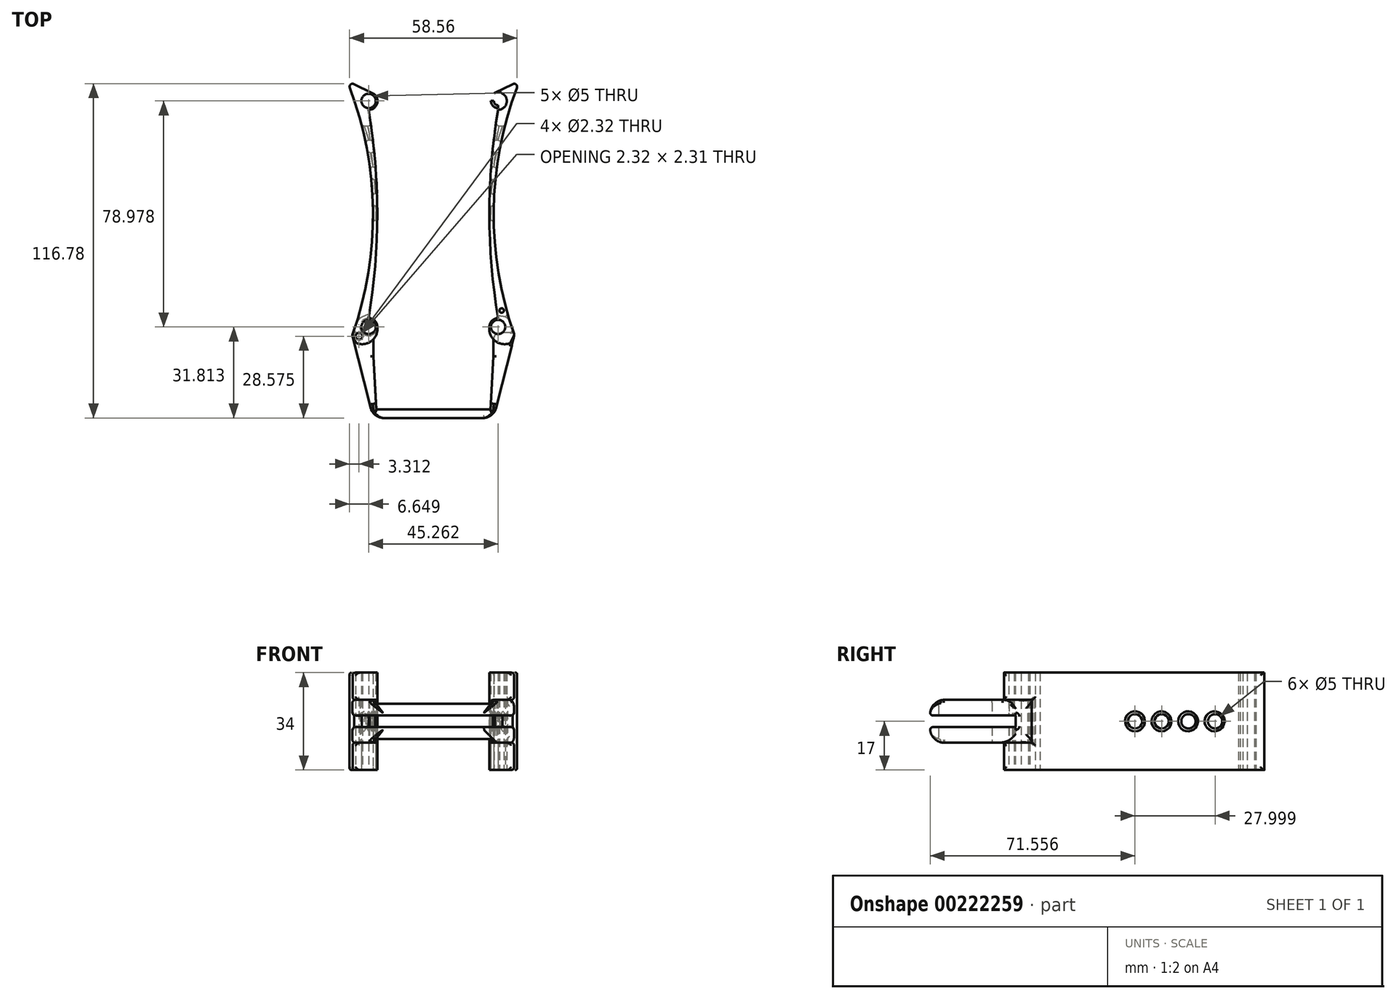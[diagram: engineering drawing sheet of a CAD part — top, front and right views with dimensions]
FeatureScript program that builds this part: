
annotation { "Feature Type Name" : "Feature", "Feature Type Description" : "" }
export const myFeature = defineFeature(function(context is Context, id is Id, definition is map)
    precondition{}
    {
        {
            var Q0;
            Q0=qCreatedBy(makeId("Top.planeOp"),FACE);
            var sketch = newSketch(context, id + "F0", { "sketchPlane" : qUnion([Q0])});
            skPoint(sketch, "E0.middle", {"position": v(-0.14, 7.73) * mm});
            skCircle(sketch, "E1", {"center": v(-22.63, 47.23) * mm, "radius": 1.5 * mm});
            skCircle(sketch, "E2", {"center": v(-22.63, -31.75) * mm, "radius": 1.5 * mm});
            skLineSegment(sketch, "E3.MirrorCS", {"start": v(-28.32, -34.53) * mm, "end": v(-26.94, -37.37) * mm});
            skPoint(sketch, "E4.orphan", {"position": v(-30.14, -38.77) * mm});
            skCircle(sketch, "E5", {"center": v(-22.63, 47.23) * mm, "radius": 2.5 * mm});
            skCircle(sketch, "E6", {"center": v(-22.63, -31.75) * mm, "radius": 2.5 * mm});
            skLineSegment(sketch, "E7.bottom", {"start": v(-22.63, 47.23) * mm, "end": v(-20.13, 47.23) * mm});
            skLineSegment(sketch, "E7.top", {"start": v(-22.63, -31.77) * mm, "end": v(-20.13, -31.77) * mm});
            skLineSegment(sketch, "E7.left", {"start": v(-22.63, 47.23) * mm, "end": v(-22.63, 44.73) * mm});
            skLineSegment(sketch, "E8.trimOffspring", {"start": v(-22.63, -29.25) * mm, "end": v(-22.63, -31.77) * mm});
            skCircle(sketch, "E9", {"center": v(-17.26, 14.85) * mm, "radius": 1.49 * mm});
            skPoint(sketch, "E10.visualSharp", {"position": v(-16.9, 52.24) * mm});
            skPoint(sketch, "E11.visualSharp", {"position": v(-16.9, -36.79) * mm});
            skPoint(sketch, "E12.orphan", {"position": v(-25.56, -40.21) * mm});
            skLineSegment(sketch, "E13", {"start": v(0, 54.23) * mm, "end": v(0, -41.79) * mm});
            skCircle(sketch, "E14", {"center": v(-22.63, -31.75) * mm, "radius": 3.07 * mm});
            skCircle(sketch, "E15", {"center": v(-22.6, 47.19) * mm, "radius": 3.07 * mm});
            skLineSegment(sketch, "E16", {"start": v(-30.13, 54.23) * mm, "end": v(-21.26, 49.95) * mm});
            skArc(sketch, "E17", {"start": v(-22.63, -28.68) * mm, "mid": v(-19.57, 7.72) * mm, "end": v(-22.63, 44.12) * mm});
            skArc(sketch, "E18", {"start": v(-28.32, -34.53) * mm, "mid": v(-21.12, 10.01) * mm, "end": v(-30.13, 54.23) * mm});
            skArc(sketch, "E19", {"start": v(-26.94, -37.37) * mm, "mid": v(-21.67, -36.68) * mm, "end": v(-19.57, -31.79) * mm});
            skCircle(sketch, "E20", {"center": v(-25.97, -34.98) * mm, "radius": 1.16 * mm});
            skLineSegment(sketch, "E21", {"start": v(-20.93, -41.99) * mm, "end": v(-21.06, -41.99) * mm});
            skLineSegment(sketch, "E22", {"start": v(-0.03, 54.43) * mm, "end": v(-0.03, -55.57) * mm});
            skLineSegment(sketch, "E23.bottom", {"start": v(17.94, -58.7) * mm, "end": v(-18, -58.7) * mm});
            skLineSegment(sketch, "E23.top", {"start": v(17.94, -25.28) * mm, "end": v(-18, -25.28) * mm});
            skLineSegment(sketch, "E23.left", {"start": v(17.94, -58.7) * mm, "end": v(17.94, -25.28) * mm});
            skLineSegment(sketch, "E23.right", {"start": v(-18, -58.7) * mm, "end": v(-18, -25.28) * mm});
            skPoint(sketch, "E23.middle", {"position": v(-0.03, -41.99) * mm});
            skLineSegment(sketch, "E24", {"start": v(-21.06, -63.6) * mm, "end": v(1.55, -63.6) * mm});
            skLineSegment(sketch, "E25", {"start": v(-19.96, -60.6) * mm, "end": v(-20.93, -41.99) * mm});
            skLineSegment(sketch, "E26", {"start": v(-19.96, -60.6) * mm, "end": v(1.54, -60.6) * mm});
            skLineSegment(sketch, "E27.MirrorCS", {"start": v(21.06, -63.6) * mm, "end": v(-0.04, -63.6) * mm});
            skLineSegment(sketch, "E28.MirrorCS", {"start": v(19.9, -60.6) * mm, "end": v(-0.03, -60.6) * mm});
            skLineSegment(sketch, "E29.MirrorCS", {"start": v(19.9, -60.6) * mm, "end": v(20.86, -41.99) * mm});
            skLineSegment(sketch, "E30", {"start": v(-28.32, -34.53) * mm, "end": v(-21.06, -63.6) * mm});
            skLineSegment(sketch, "E31", {"start": v(-20.93, -41.99) * mm, "end": v(-20.93, -36) * mm});
            skLineSegment(sketch, "E32.MirrorCS", {"start": v(21.06, -63.6) * mm, "end": v(-1.55, -63.6) * mm});
            skLineSegment(sketch, "E33.MirrorCS", {"start": v(22.63, 47.23) * mm, "end": v(20.13, 47.23) * mm});
            skLineSegment(sketch, "E34.MirrorCS", {"start": v(22.63, -31.77) * mm, "end": v(20.13, -31.77) * mm});
            skLineSegment(sketch, "E35.MirrorCS", {"start": v(22.63, 47.23) * mm, "end": v(22.63, 44.73) * mm});
            skLineSegment(sketch, "E36.MirrorCS", {"start": v(22.63, -29.25) * mm, "end": v(22.63, -31.77) * mm});
            skCircle(sketch, "E37.MirrorC", {"center": v(22.63, 47.23) * mm, "radius": 1.5 * mm});
            skCircle(sketch, "E38.MirrorC", {"center": v(22.63, -31.75) * mm, "radius": 1.5 * mm});
            skLineSegment(sketch, "E39.MirrorCS", {"start": v(28.32, -34.53) * mm, "end": v(26.94, -37.37) * mm});
            skLineSegment(sketch, "E40.MirrorCS", {"start": v(20.93, -41.99) * mm, "end": v(21.06, -41.99) * mm});
            skCircle(sketch, "E41.MirrorC", {"center": v(22.63, 47.23) * mm, "radius": 2.5 * mm});
            skCircle(sketch, "E42.MirrorC", {"center": v(22.63, -31.75) * mm, "radius": 2.5 * mm});
            skArc(sketch, "E43.MirrorCS", {"start": v(26.94, -37.37) * mm, "mid": v(21.67, -36.68) * mm, "end": v(19.57, -31.79) * mm});
            skCircle(sketch, "E44.MirrorC", {"center": v(17.26, 14.85) * mm, "radius": 1.49 * mm});
            skPoint(sketch, "E45.MirrorP", {"position": v(30.14, -38.77) * mm});
            skCircle(sketch, "E46.MirrorC", {"center": v(22.6, 47.19) * mm, "radius": 3.07 * mm});
            skLineSegment(sketch, "E47.MirrorCS", {"start": v(20.93, -41.99) * mm, "end": v(20.93, -36) * mm});
            skCircle(sketch, "E48.MirrorC", {"center": v(22.63, -31.75) * mm, "radius": 3.07 * mm});
            skPoint(sketch, "E49.MirrorP", {"position": v(16.9, -36.79) * mm});
            skPoint(sketch, "E50.MirrorP", {"position": v(16.9, 52.24) * mm});
            skLineSegment(sketch, "E51.MirrorCS", {"start": v(30.13, 54.23) * mm, "end": v(21.26, 49.95) * mm});
            skArc(sketch, "E52.MirrorCS", {"start": v(28.32, -34.53) * mm, "mid": v(21.12, 10.01) * mm, "end": v(30.13, 54.23) * mm});
            skArc(sketch, "E53.MirrorCS", {"start": v(22.63, -28.68) * mm, "mid": v(19.57, 7.72) * mm, "end": v(22.63, 44.12) * mm});
            skLineSegment(sketch, "E54.MirrorCS", {"start": v(28.32, -34.53) * mm, "end": v(21.06, -63.6) * mm});
            skPoint(sketch, "E55.MirrorP", {"position": v(25.56, -40.21) * mm});
            skLineSegment(sketch, "E56.MirrorCS", {"start": v(19.96, -60.6) * mm, "end": v(-1.54, -60.6) * mm});
            skLineSegment(sketch, "E57.MirrorCS", {"start": v(19.96, -60.6) * mm, "end": v(20.93, -41.99) * mm});
            skLineSegment(sketch, "E58", {"start": v(-22.37, -27.13) * mm, "end": v(-25.55, -28.61) * mm});
            skLineSegment(sketch, "E59", {"start": v(-25.55, -28.61) * mm, "end": v(-26.89, -30.25) * mm});
            skLineSegment(sketch, "E60", {"start": v(20.83, -29.27) * mm, "end": v(21.44, -29.55) * mm});
            skLineSegment(sketch, "E61", {"start": v(21.5, -34.6) * mm, "end": v(22.1, -34.2) * mm});
            skLineSegment(sketch, "E62", {"start": v(20.66, -29.4) * mm, "end": v(22.63, -27.74) * mm});
            skLineSegment(sketch, "E63", {"start": v(22.63, -27.74) * mm, "end": v(26.28, -28.27) * mm});
            skLineSegment(sketch, "E64", {"start": v(21.5, -34.6) * mm, "end": v(20.93, -36) * mm});
            skCircle(sketch, "E65", {"center": v(23.85, -26) * mm, "radius": 0.78 * mm});
            skSolve(sketch);
        }
        {
            var Q0;
            Q0=makeQuery(id+"F0.imprint","IMPRINT",FACE,{"disambiguationData":[TD([[makeQuery(id+"F0.imprint","IMPRINT",EDGE,{"derivedFrom":sQuery(id+"F0.wireOp",EDGE,"E3.MirrorCS")}),1.0]])]});
            var Q1;
            {var subQ0=sQuery(id+"F0.wireOp",EDGE,"E6");var subQ1=makeQuery(id+"F0.imprint","INTERSECT",VERTEX,{"derivedFrom":[subQ0,sQuery(id+"F0.wireOp",EDGE,"E7.top")]});Q1=makeQuery(id+"F0.imprint","IMPRINT",FACE,{"disambiguationData":[TD([[makeQuery(id+"F0.imprint","IMPRINT",EDGE,{"disambiguationData":[TD([[subQ1,1.0]])],"derivedFrom":subQ0}),-1.0]])]});}
            var Q2;
            {var subQ0=sQuery(id+"F0.wireOp",EDGE,"E5");var subQ1=makeQuery(id+"F0.imprint","INTERSECT",VERTEX,{"derivedFrom":[subQ0,sQuery(id+"F0.wireOp",EDGE,"E7.bottom")]});Q2=makeQuery(id+"F0.imprint","IMPRINT",FACE,{"disambiguationData":[TD([[makeQuery(id+"F0.imprint","IMPRINT",EDGE,{"disambiguationData":[TD([[subQ1,-1.0]])],"derivedFrom":subQ0}),-1.0]])]});}
            var Q3;
            {var subQ1=sQuery(id+"F0.wireOp",EDGE,"E16");Q3=makeQuery(id+"F0.imprint","IMPRINT",FACE,{"disambiguationData":[TD([[makeQuery(id+"F0.imprint","IMPRINT",EDGE,{"derivedFrom":subQ1}),-1.0]])]});}
            var Q4;
            {var subQ6=sQuery(id+"F0.wireOp",EDGE,"E51.MirrorCS");Q4=makeQuery(id+"F0.imprint","IMPRINT",FACE,{"disambiguationData":[TD([[makeQuery(id+"F0.imprint","IMPRINT",EDGE,{"derivedFrom":subQ6}),1.0]])]});}
            var Q5;
            {var subQ0=sQuery(id+"F0.wireOp",EDGE,"E41.MirrorC");var subQ1=makeQuery(id+"F0.imprint","INTERSECT",VERTEX,{"derivedFrom":[sQuery(id+"F0.wireOp",EDGE,"E33.MirrorCS"),subQ0]});Q5=makeQuery(id+"F0.imprint","IMPRINT",FACE,{"disambiguationData":[TD([[makeQuery(id+"F0.imprint","IMPRINT",EDGE,{"disambiguationData":[TD([[subQ1,-1.0]])],"derivedFrom":subQ0}),1.0]])]});}
            var Q6;
            {var subQ1=sQuery(id+"F0.wireOp",EDGE,"E39.MirrorCS");Q6=makeQuery(id+"F0.imprint","IMPRINT",FACE,{"disambiguationData":[TD([[makeQuery(id+"F0.imprint","IMPRINT",EDGE,{"derivedFrom":subQ1}),-1.0]])]});}
            var Q7;
            {var subQ3=sQuery(id+"F0.wireOp",EDGE,"E60");Q7=makeQuery(id+"F0.imprint","IMPRINT",FACE,{"disambiguationData":[TD([[makeQuery(id+"F0.imprint","IMPRINT",EDGE,{"derivedFrom":subQ3}),1.0]])]});}
            var Q8;
            {var subQ3=sQuery(id+"F0.wireOp",EDGE,"E60");Q8=makeQuery(id+"F0.imprint","IMPRINT",FACE,{"disambiguationData":[TD([[makeQuery(id+"F0.imprint","IMPRINT",EDGE,{"derivedFrom":subQ3}),-1.0]])]});}
            var Q9;
            {var subQ0=sQuery(id+"F0.wireOp",EDGE,"E48.MirrorC");var subQ1=makeQuery(id+"F0.imprint","INTERSECT",VERTEX,{"derivedFrom":[subQ0,sQuery(id+"F0.wireOp",EDGE,"E60")]});Q9=makeQuery(id+"F0.imprint","IMPRINT",FACE,{"disambiguationData":[TD([[makeQuery(id+"F0.imprint","IMPRINT",EDGE,{"disambiguationData":[TD([[subQ1,1.0]])],"derivedFrom":subQ0}),1.0]])]});}
            var Q10;
            {var subQ3=sQuery(id+"F0.wireOp",EDGE,"E64");Q10=makeQuery(id+"F0.imprint","IMPRINT",FACE,{"disambiguationData":[TD([[makeQuery(id+"F0.imprint","IMPRINT",EDGE,{"derivedFrom":subQ3}),-1.0]])]});}
            extrude(context, id + "F1", {"entities" : qUnion([Q0, Q1, Q2, Q3, Q4, Q5, Q6, Q7, Q8, Q9, Q10]), "endBound" : BoundingType.SYMMETRIC, "depth" : 34 * mm});
        }
        {
            var Q0;
            {var subQ0=sQuery(id+"F0.wireOp",EDGE,"E6");var subQ1=makeQuery(id+"F0.imprint","INTERSECT",VERTEX,{"derivedFrom":[subQ0,sQuery(id+"F0.wireOp",EDGE,"E7.top")]});Q0=makeQuery(id+"F0.imprint","IMPRINT",FACE,{"disambiguationData":[TD([[makeQuery(id+"F0.imprint","IMPRINT",EDGE,{"disambiguationData":[TD([[subQ1,1.0]])],"derivedFrom":subQ0}),-1.0]])]});}
            var Q1;
            {var subQ1=sQuery(id+"F0.wireOp",EDGE,"E3.MirrorCS");Q1=makeQuery(id+"F0.imprint","IMPRINT",FACE,{"disambiguationData":[TD([[makeQuery(id+"F0.imprint","IMPRINT",EDGE,{"derivedFrom":subQ1}),1.0]])]});}
            var Q2;
            {var subQ0=sQuery(id+"F0.wireOp",EDGE,"E48.MirrorC");var subQ1=makeQuery(id+"F0.imprint","INTERSECT",VERTEX,{"derivedFrom":[subQ0,sQuery(id+"F0.wireOp",EDGE,"E60")]});Q2=makeQuery(id+"F0.imprint","IMPRINT",FACE,{"disambiguationData":[TD([[makeQuery(id+"F0.imprint","IMPRINT",EDGE,{"disambiguationData":[TD([[subQ1,1.0]])],"derivedFrom":subQ0}),1.0]])]});}
            var Q3;
            {var subQ1=sQuery(id+"F0.wireOp",EDGE,"E39.MirrorCS");Q3=makeQuery(id+"F0.imprint","IMPRINT",FACE,{"disambiguationData":[TD([[makeQuery(id+"F0.imprint","IMPRINT",EDGE,{"derivedFrom":subQ1}),-1.0]])]});}
            var Q4;
            {var subQ3=sQuery(id+"F0.wireOp",EDGE,"E60");Q4=makeQuery(id+"F0.imprint","IMPRINT",FACE,{"disambiguationData":[TD([[makeQuery(id+"F0.imprint","IMPRINT",EDGE,{"derivedFrom":subQ3}),1.0]])]});}
            var Q5;
            {var subQ3=sQuery(id+"F0.wireOp",EDGE,"E64");Q5=makeQuery(id+"F0.imprint","IMPRINT",FACE,{"disambiguationData":[TD([[makeQuery(id+"F0.imprint","IMPRINT",EDGE,{"derivedFrom":subQ3}),-1.0]])]});}
            var Q6;
            {var subQ3=sQuery(id+"F0.wireOp",EDGE,"E60");Q6=makeQuery(id+"F0.imprint","IMPRINT",FACE,{"disambiguationData":[TD([[makeQuery(id+"F0.imprint","IMPRINT",EDGE,{"derivedFrom":subQ3}),-1.0]])]});}
            extrude(context, id + "F2", {"entities" : qUnion([Q0, Q1, Q2, Q3, Q4, Q5, Q6]), "operationType" : NewBodyOperationType.REMOVE, "endBound" : BoundingType.SYMMETRIC, "depth" : 15 * mm});
        }
        {
            var Q0;
            {var subQ1=sQuery(id+"F0.wireOp",EDGE,"E3.MirrorCS");Q0=makeQuery(id+"F0.imprint","IMPRINT",FACE,{"disambiguationData":[TD([[makeQuery(id+"F0.imprint","IMPRINT",EDGE,{"derivedFrom":subQ1}),1.0]])]});}
            var Q1;
            {var subQ4=sQuery(id+"F0.wireOp",EDGE,"E3.MirrorCS");Q1=makeQuery(id+"F0.imprint","IMPRINT",FACE,{"disambiguationData":[TD([[makeQuery(id+"F0.imprint","IMPRINT",EDGE,{"derivedFrom":subQ4}),-1.0]])]});}
            var Q2;
            {var subQ1=sQuery(id+"F0.wireOp",EDGE,"E39.MirrorCS");Q2=makeQuery(id+"F0.imprint","IMPRINT",FACE,{"disambiguationData":[TD([[makeQuery(id+"F0.imprint","IMPRINT",EDGE,{"derivedFrom":subQ1}),-1.0]])]});}
            var Q3;
            {var subQ0=sQuery(id+"F0.wireOp",EDGE,"E48.MirrorC");var subQ1=makeQuery(id+"F0.imprint","INTERSECT",VERTEX,{"derivedFrom":[subQ0,sQuery(id+"F0.wireOp",EDGE,"E60")]});Q3=makeQuery(id+"F0.imprint","IMPRINT",FACE,{"disambiguationData":[TD([[makeQuery(id+"F0.imprint","IMPRINT",EDGE,{"disambiguationData":[TD([[subQ1,1.0]])],"derivedFrom":subQ0}),1.0]])]});}
            var Q4;
            {var subQ3=sQuery(id+"F0.wireOp",EDGE,"E60");Q4=makeQuery(id+"F0.imprint","IMPRINT",FACE,{"disambiguationData":[TD([[makeQuery(id+"F0.imprint","IMPRINT",EDGE,{"derivedFrom":subQ3}),1.0]])]});}
            extrude(context, id + "F3", {"entities" : qUnion([Q0, Q1, Q2, Q3, Q4]), "endBound" : BoundingType.SYMMETRIC, "depth" : 15 * mm});
        }
        {
            var Q0;
            Q0=makeQuery(id+"F3.opExtrude","SWEPT_FACE",FACE,{"disambiguationData":[OSD([sQuery(id+"F0.wireOp",EDGE,"E24"),sQuery(id+"F0.wireOp",EDGE,"E32.MirrorCS")])]});
            fillet(context, id + "F4", {"entities" : qUnion([Q0]), "radius" : 5 * mm, "tangentPropagation" : true, "allowEdgeOverflow" : false});
        }
        {
            var Q0;
            Q0=makeQuery(id+"F3.opExtrude","CAP_EDGE",EDGE,{"disambiguationData":[OSD([sQuery(id+"F0.wireOp",EDGE,"E57.MirrorCS")])],"isStart":false});
            var Q1;
            Q1=makeQuery(id+"F3.opExtrude","CAP_EDGE",EDGE,{"disambiguationData":[OSD([sQuery(id+"F0.wireOp",EDGE,"E54.MirrorCS")])],"isStart":false});
            var Q2;
            Q2=makeQuery(id+"F3.opExtrude","CAP_EDGE",EDGE,{"disambiguationData":[OSD([sQuery(id+"F0.wireOp",EDGE,"E25")])],"isStart":false});
            var Q3;
            Q3=makeQuery(id+"F3.opExtrude","CAP_EDGE",EDGE,{"disambiguationData":[OSD([sQuery(id+"F0.wireOp",EDGE,"E30")])],"isStart":false});
            var Q4;
            Q4=makeQuery(id+"F3.opExtrude","CAP_EDGE",EDGE,{"disambiguationData":[OSD([sQuery(id+"F0.wireOp",EDGE,"E30")])],"isStart":true});
            var Q5;
            Q5=makeQuery(id+"F3.opExtrude","CAP_EDGE",EDGE,{"disambiguationData":[OSD([sQuery(id+"F0.wireOp",EDGE,"E25")])],"isStart":true});
            var Q6;
            Q6=makeQuery(id+"F3.opExtrude","CAP_EDGE",EDGE,{"disambiguationData":[OSD([sQuery(id+"F0.wireOp",EDGE,"E31")])],"isStart":true});
            var Q7;
            Q7=makeQuery(id+"F4.opFillet","BLEND_EDGE",EDGE,{"blendedFrom":[makeQuery(id+"F3.opExtrude","CAP_EDGE",EDGE,{"disambiguationData":[OSD([sQuery(id+"F0.wireOp",EDGE,"E24"),sQuery(id+"F0.wireOp",EDGE,"E32.MirrorCS")])],"isStart":true}),makeQuery(id+"F3.opExtrude","SWEPT_FACE",FACE,{"disambiguationData":[OSD([sQuery(id+"F0.wireOp",EDGE,"E26"),sQuery(id+"F0.wireOp",EDGE,"E56.MirrorCS")])]})],"blendedInto":[makeQuery(id+"F3.opExtrude","SWEPT_FACE",FACE,{"disambiguationData":[OSD([sQuery(id+"F0.wireOp",EDGE,"E26"),sQuery(id+"F0.wireOp",EDGE,"E56.MirrorCS")])]})]});
            var Q8;
            Q8=makeQuery(id+"F3.opExtrude","CAP_EDGE",EDGE,{"disambiguationData":[OSD([sQuery(id+"F0.wireOp",EDGE,"E57.MirrorCS")])],"isStart":true});
            var Q9;
            Q9=makeQuery(id+"F3.opExtrude","SWEPT_EDGE",EDGE,{"disambiguationData":[OSD([sQuery(id+"F0.wireOp",EDGE,"E3.MirrorCS"),sQuery(id+"F0.wireOp",EDGE,"E18"),sQuery(id+"F0.wireOp",EDGE,"E30")])]});
            var Q10;
            Q10=makeQuery(id+"F4.opFillet","BLEND_EDGE",EDGE,{"blendedFrom":[makeQuery(id+"F3.opExtrude","CAP_EDGE",EDGE,{"disambiguationData":[OSD([sQuery(id+"F0.wireOp",EDGE,"E24"),sQuery(id+"F0.wireOp",EDGE,"E32.MirrorCS")])],"isStart":false}),makeQuery(id+"F3.opExtrude","SWEPT_FACE",FACE,{"disambiguationData":[OSD([sQuery(id+"F0.wireOp",EDGE,"E26"),sQuery(id+"F0.wireOp",EDGE,"E56.MirrorCS")])]})],"blendedInto":[makeQuery(id+"F3.opExtrude","SWEPT_FACE",FACE,{"disambiguationData":[OSD([sQuery(id+"F0.wireOp",EDGE,"E26"),sQuery(id+"F0.wireOp",EDGE,"E56.MirrorCS")])]})]});
            fillet(context, id + "F5", {"entities" : qUnion([Q0, Q1, Q2, Q3, Q4, Q5, Q6, Q7, Q8, Q9, Q10]), "radius" : 1 * mm, "tangentPropagation" : true, "allowEdgeOverflow" : false});
        }
        {
            var Q0;
            Q0=qCreatedBy(makeId("Right.planeOp"),FACE);
            var sketch = newSketch(context, id + "F6", { "sketchPlane" : qUnion([Q0])});
            skCircle(sketch, "E66", {"center": v(36, 0) * mm, "radius": 2.5 * mm});
            skCircle(sketch, "E67", {"center": v(26.66, 0) * mm, "radius": 2.5 * mm});
            skCircle(sketch, "E68", {"center": v(17.33, 0) * mm, "radius": 2.5 * mm});
            skCircle(sketch, "E69", {"center": v(8, 0) * mm, "radius": 2.5 * mm});
            skSolve(sketch);
        }
        {
            var Q0;
            Q0=makeQuery(id+"F6.imprint","IMPRINT",FACE,{"disambiguationData":[TD([[makeQuery(id+"F6.imprint","IMPRINT",EDGE,{"derivedFrom":sQuery(id+"F6.wireOp",EDGE,"E66")}),1.0]])]});
            var Q1;
            Q1=makeQuery(id+"F6.imprint","IMPRINT",FACE,{"disambiguationData":[TD([[makeQuery(id+"F6.imprint","IMPRINT",EDGE,{"derivedFrom":sQuery(id+"F6.wireOp",EDGE,"E67")}),1.0]])]});
            var Q2;
            Q2=makeQuery(id+"F6.imprint","IMPRINT",FACE,{"disambiguationData":[TD([[makeQuery(id+"F6.imprint","IMPRINT",EDGE,{"derivedFrom":sQuery(id+"F6.wireOp",EDGE,"E68")}),1.0]])]});
            var Q3;
            Q3=makeQuery(id+"F6.imprint","IMPRINT",FACE,{"disambiguationData":[TD([[makeQuery(id+"F6.imprint","IMPRINT",EDGE,{"derivedFrom":sQuery(id+"F6.wireOp",EDGE,"E69")}),1.0]])]});
            var Q4;
            Q4=sQuery(id+"F6.wireOp",EDGE,"E66");
            var Q5;
            Q5=sQuery(id+"F6.wireOp",EDGE,"E67");
            var Q6;
            Q6=sQuery(id+"F6.wireOp",EDGE,"E68");
            var Q7;
            Q7=sQuery(id+"F6.wireOp",EDGE,"E69");
            extrude(context, id + "F7", {"entities" : qUnion([Q0, Q1, Q2, Q3]), "operationType" : NewBodyOperationType.REMOVE, "surfaceEntities" : qUnion([Q4, Q5, Q6, Q7]), "endBound" : BoundingType.SYMMETRIC, "oppositeDirection" : true, "depth" : 70 * mm});
        }
        {
            var Q0;
            {var subQ0=sQuery(id+"F0.wireOp",EDGE,"E20");var subQ1=sQuery(id+"F0.wireOp",EDGE,"E19");var subQ2=sQuery(id+"F0.wireOp",EDGE,"E18");var subQ3=sQuery(id+"F0.wireOp",EDGE,"E17");var subQ4=sQuery(id+"F0.wireOp",EDGE,"E14");var subQ5=sQuery(id+"F0.wireOp",EDGE,"E6");var subQ6=sQuery(id+"F0.wireOp",EDGE,"E3.MirrorCS");Q0=makeQuery(id+"F2.boolean.opBoolean","SPLIT",FACE,{"disambiguationData":[TD([makeQuery(id+"F2.opExtrude","CAP_FACE",FACE,{"disambiguationData":[OSD([subQ6,subQ5,subQ4,subQ3,subQ2,subQ1,subQ0,sQuery(id+"F0.wireOp",EDGE,"E58"),sQuery(id+"F0.wireOp",EDGE,"E59")])],"isStart":false})])],"derivedFrom":makeQuery(id+"F1.opExtrude","SWEPT_FACE",FACE,{"disambiguationData":[OSD([subQ6])]})});}
            var Q1;
            {var subQ0=sQuery(id+"F0.wireOp",EDGE,"E20");var subQ1=sQuery(id+"F0.wireOp",EDGE,"E19");var subQ2=sQuery(id+"F0.wireOp",EDGE,"E18");var subQ3=sQuery(id+"F0.wireOp",EDGE,"E17");var subQ4=sQuery(id+"F0.wireOp",EDGE,"E14");var subQ5=sQuery(id+"F0.wireOp",EDGE,"E6");var subQ6=sQuery(id+"F0.wireOp",EDGE,"E3.MirrorCS");Q1=makeQuery(id+"F2.boolean.opBoolean","SPLIT",FACE,{"disambiguationData":[TD([makeQuery(id+"F2.opExtrude","CAP_FACE",FACE,{"disambiguationData":[OSD([subQ6,subQ5,subQ4,subQ3,subQ2,subQ1,subQ0,sQuery(id+"F0.wireOp",EDGE,"E58"),sQuery(id+"F0.wireOp",EDGE,"E59")])],"isStart":true})])],"derivedFrom":makeQuery(id+"F1.opExtrude","SWEPT_FACE",FACE,{"disambiguationData":[OSD([subQ6])]})});}
            var Q2;
            Q2=makeQuery(id+"F1.opExtrude","SWEPT_FACE",FACE,{"disambiguationData":[OSD([sQuery(id+"F0.wireOp",EDGE,"E18")])]});
            fillet(context, id + "F8", {"entities" : qUnion([Q0, Q1, Q2]), "radius" : 1 * mm, "tangentPropagation" : true, "allowEdgeOverflow" : false});
        }
        {
            var Q0;
            Q0=makeQuery(id+"F1.opExtrude","SWEPT_FACE",FACE,{"disambiguationData":[OSD([sQuery(id+"F0.wireOp",EDGE,"E52.MirrorCS")])]});
            var Q1;
            {var subQ0=sQuery(id+"F0.wireOp",EDGE,"E62");var subQ1=sQuery(id+"F0.wireOp",EDGE,"E52.MirrorCS");var subQ2=sQuery(id+"F0.wireOp",EDGE,"E48.MirrorC");var subQ3=sQuery(id+"F0.wireOp",EDGE,"E43.MirrorCS");var subQ4=sQuery(id+"F0.wireOp",EDGE,"E42.MirrorC");var subQ5=sQuery(id+"F0.wireOp",EDGE,"E39.MirrorCS");Q1=makeQuery(id+"F2.boolean.opBoolean","SPLIT",FACE,{"disambiguationData":[TD([makeQuery(id+"F2.opExtrude","CAP_FACE",FACE,{"disambiguationData":[OSD([subQ5,subQ4,subQ3,subQ2,subQ1,subQ0,sQuery(id+"F0.wireOp",EDGE,"E63")])],"isStart":false})])],"derivedFrom":makeQuery(id+"F1.opExtrude","SWEPT_FACE",FACE,{"disambiguationData":[OSD([subQ5])]})});}
            var Q2;
            {var subQ0=sQuery(id+"F0.wireOp",EDGE,"E62");var subQ1=sQuery(id+"F0.wireOp",EDGE,"E52.MirrorCS");var subQ2=sQuery(id+"F0.wireOp",EDGE,"E48.MirrorC");var subQ3=sQuery(id+"F0.wireOp",EDGE,"E43.MirrorCS");var subQ4=sQuery(id+"F0.wireOp",EDGE,"E42.MirrorC");var subQ5=sQuery(id+"F0.wireOp",EDGE,"E39.MirrorCS");Q2=makeQuery(id+"F2.boolean.opBoolean","SPLIT",FACE,{"disambiguationData":[TD([makeQuery(id+"F2.opExtrude","CAP_FACE",FACE,{"disambiguationData":[OSD([subQ5,subQ4,subQ3,subQ2,subQ1,subQ0,sQuery(id+"F0.wireOp",EDGE,"E63")])],"isStart":true})])],"derivedFrom":makeQuery(id+"F1.opExtrude","SWEPT_FACE",FACE,{"disambiguationData":[OSD([subQ5])]})});}
            fillet(context, id + "F9", {"entities" : qUnion([Q0, Q1, Q2]), "radius" : 1 * mm, "tangentPropagation" : true, "allowEdgeOverflow" : false});
        }
        {
            var Q0;
            Q0=makeQuery(id+"F3.opExtrude","SWEPT_FACE",FACE,{"disambiguationData":[OSD([sQuery(id+"F0.wireOp",EDGE,"E52.MirrorCS")])]});
            fillet(context, id + "F10", {"entities" : qUnion([Q0]), "radius" : 3 * mm, "tangentPropagation" : true, "allowEdgeOverflow" : false});
        }
        {
            var Q0;
            Q0=makeQuery(id+"F3.opExtrude","SWEPT_FACE",FACE,{"disambiguationData":[OSD([sQuery(id+"F0.wireOp",EDGE,"E18")])]});
            var Q1;
            Q1=makeQuery(id+"F3.opExtrude","SWEPT_FACE",FACE,{"disambiguationData":[OSD([sQuery(id+"F0.wireOp",EDGE,"E59")])]});
            fillet(context, id + "F11", {"entities" : qUnion([Q0, Q1]), "radius" : 1 * mm, "tangentPropagation" : true, "allowEdgeOverflow" : false});
        }
        {
            var Q0;
            Q0=makeQuery(id+"F7.boolean.opBoolean","INTERSECT",EDGE,{"derivedFrom":[makeQuery(id+"F1.opExtrude","SWEPT_FACE",FACE,{"disambiguationData":[OSD([sQuery(id+"F0.wireOp",EDGE,"E17")])]}),makeQuery(id+"F7.opExtrude","SWEPT_FACE",FACE,{"disambiguationData":[OSD([sQuery(id+"F6.wireOp",EDGE,"E66")])]})]});
            var Q1;
            Q1=makeQuery(id+"F7.boolean.opBoolean","INTERSECT",EDGE,{"derivedFrom":[makeQuery(id+"F1.opExtrude","SWEPT_FACE",FACE,{"disambiguationData":[OSD([sQuery(id+"F0.wireOp",EDGE,"E17")])]}),makeQuery(id+"F7.opExtrude","SWEPT_FACE",FACE,{"disambiguationData":[OSD([sQuery(id+"F6.wireOp",EDGE,"E67")])]})]});
            fillet(context, id + "F12", {"entities" : qUnion([Q0, Q1]), "radius" : 1 * mm, "tangentPropagation" : true, "allowEdgeOverflow" : false});
        }
        {
            var Q0;
            Q0=makeQuery(id+"F7.boolean.opBoolean","INTERSECT",EDGE,{"derivedFrom":[makeQuery(id+"F1.opExtrude","SWEPT_FACE",FACE,{"disambiguationData":[OSD([sQuery(id+"F0.wireOp",EDGE,"E53.MirrorCS")])]}),makeQuery(id+"F7.opExtrude","SWEPT_FACE",FACE,{"disambiguationData":[OSD([sQuery(id+"F6.wireOp",EDGE,"E66")])]})]});
            var Q1;
            Q1=makeQuery(id+"F7.boolean.opBoolean","INTERSECT",EDGE,{"derivedFrom":[makeQuery(id+"F1.opExtrude","SWEPT_FACE",FACE,{"disambiguationData":[OSD([sQuery(id+"F0.wireOp",EDGE,"E53.MirrorCS")])]}),makeQuery(id+"F7.opExtrude","SWEPT_FACE",FACE,{"disambiguationData":[OSD([sQuery(id+"F6.wireOp",EDGE,"E67")])]})]});
            fillet(context, id + "F13", {"entities" : qUnion([Q0, Q1]), "radius" : 1 * mm, "tangentPropagation" : true, "allowEdgeOverflow" : false});
        }
        {
            var Q0;
            Q0=qCreatedBy(makeId("Right.planeOp"),FACE);
            var sketch = newSketch(context, id + "F14", { "sketchPlane" : qUnion([Q0])});
            skLineSegment(sketch, "E70.bottom", {"start": v(-63.94, -2.01) * mm, "end": v(-34, -2.01) * mm});
            skLineSegment(sketch, "E70.top", {"start": v(-63.94, 2.01) * mm, "end": v(-34, 2.01) * mm});
            skLineSegment(sketch, "E70.left", {"start": v(-63.94, -2.01) * mm, "end": v(-63.94, 2.01) * mm});
            skLineSegment(sketch, "E70.right", {"start": v(-33.7, -1.7) * mm, "end": v(-33.7, 1.7) * mm});
            skPoint(sketch, "E70.middle", {"position": v(-48.82, 0) * mm});
            skPoint(sketch, "E71.visualSharp", {"position": v(-33.7, -2.01) * mm});
            skArc(sketch, "E71.filletArc", {"start": v(-34, -2.01) * mm, "mid": v(-33.79, -1.92) * mm, "end": v(-33.7, -1.7) * mm});
            skPoint(sketch, "E72.visualSharp", {"position": v(-33.7, 2.01) * mm});
            skArc(sketch, "E72.filletArc", {"start": v(-33.7, 1.7) * mm, "mid": v(-33.79, 1.92) * mm, "end": v(-34, 2.01) * mm});
            skSolve(sketch);
        }
        {
            var Q0;
            Q0=makeQuery(id+"F14.imprint","IMPRINT",FACE,{"disambiguationData":[TD([[makeQuery(id+"F14.imprint","IMPRINT",EDGE,{"derivedFrom":sQuery(id+"F14.wireOp",EDGE,"E70.bottom")}),1.0]])]});
            extrude(context, id + "F15", {"entities" : qUnion([Q0]), "operationType" : NewBodyOperationType.REMOVE, "endBound" : BoundingType.SYMMETRIC, "depth" : 60 * mm});
        }
        {
            var Q0;
            Q0=makeQuery(id+"F15.boolean.opBoolean","INTERSECT",EDGE,{"derivedFrom":[makeQuery(id+"F3.opExtrude","SWEPT_FACE",FACE,{"disambiguationData":[OSD([sQuery(id+"F0.wireOp",EDGE,"E30")])]}),makeQuery(id+"F15.opExtrude","SWEPT_FACE",FACE,{"disambiguationData":[OSD([sQuery(id+"F14.wireOp",EDGE,"E70.bottom")])]})]});
            fillet(context, id + "F16", {"entities" : qUnion([Q0]), "radius" : 1 * mm, "tangentPropagation" : true, "allowEdgeOverflow" : false});
        }
    });
